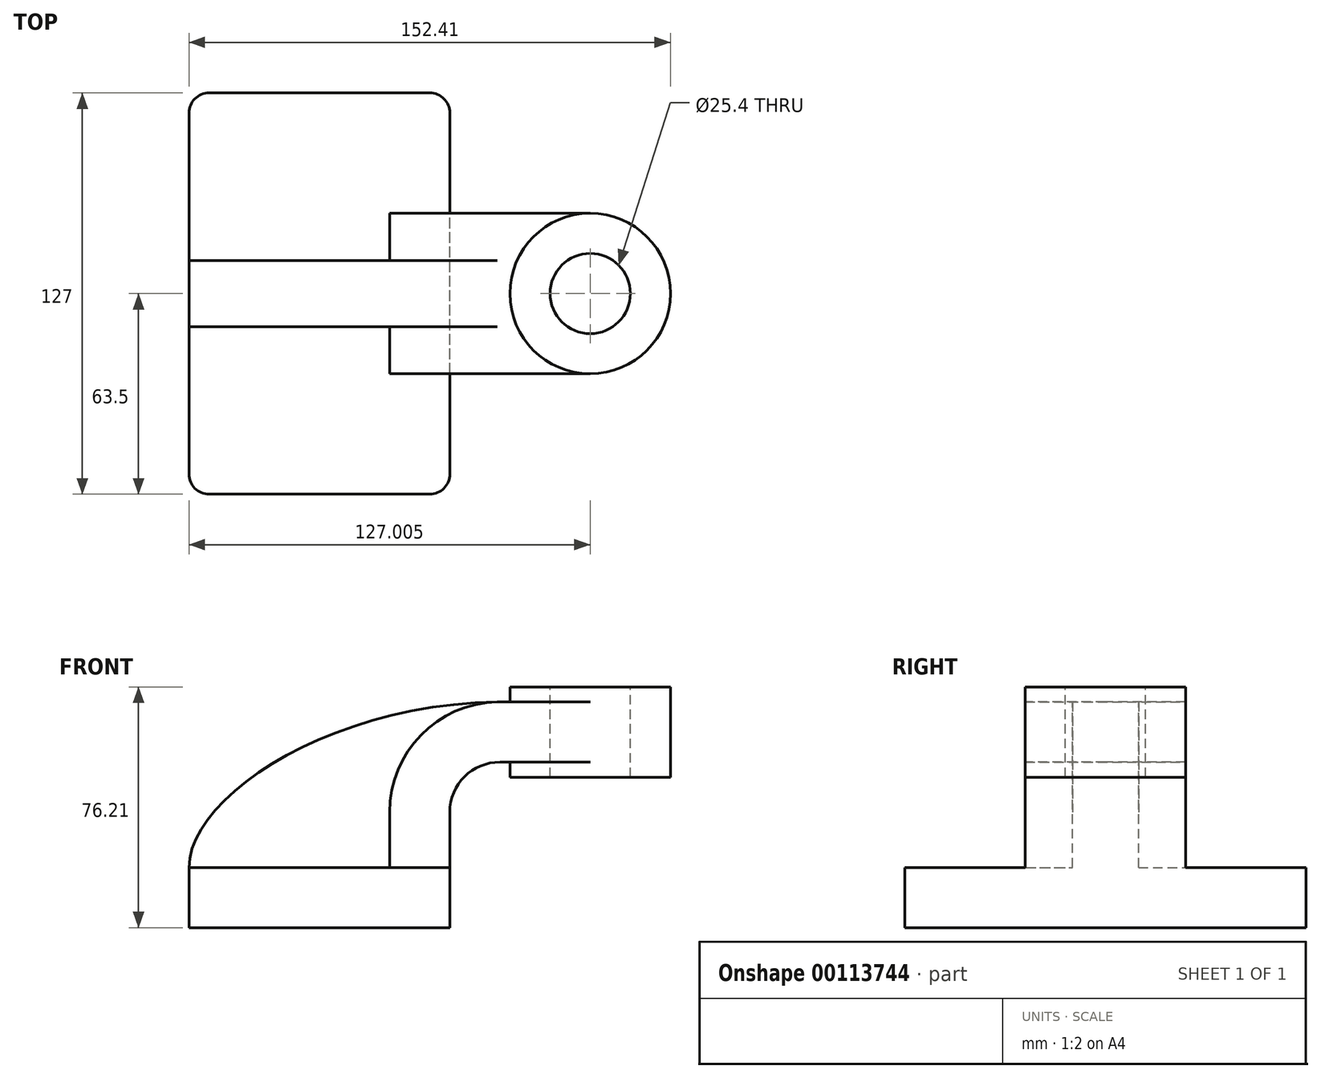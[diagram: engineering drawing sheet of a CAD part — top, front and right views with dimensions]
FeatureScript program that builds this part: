
annotation { "Feature Type Name" : "Feature", "Feature Type Description" : "" }
export const myFeature = defineFeature(function(context is Context, id is Id, definition is map)
    precondition{}
    {
        {
            var Q0;
            Q0=qCreatedBy(makeId("Front.planeOp"),FACE);
            var sketch = newSketch(context, id + "F0", { "sketchPlane" : qUnion([Q0])});
            skLineSegment(sketch, "E0.bottom", {"start": v(-41.28, -9.53) * mm, "end": v(41.28, -9.53) * mm});
            skLineSegment(sketch, "E0.top", {"start": v(-41.28, 9.53) * mm, "end": v(41.28, 9.53) * mm});
            skLineSegment(sketch, "E0.left", {"start": v(-41.28, -9.53) * mm, "end": v(-41.28, 9.53) * mm});
            skLineSegment(sketch, "E0.right", {"start": v(41.28, -9.53) * mm, "end": v(41.28, 9.53) * mm});
            skPoint(sketch, "E0.middle", {"position": v(0, 0) * mm});
            skLineSegment(sketch, "E1.bottom", {"start": v(60.32, 38.1) * mm, "end": v(111.12, 38.1) * mm});
            skLineSegment(sketch, "E1.top", {"start": v(60.32, 66.67) * mm, "end": v(111.12, 66.67) * mm});
            skLineSegment(sketch, "E1.left", {"start": v(60.32, 38.1) * mm, "end": v(60.32, 66.67) * mm});
            skLineSegment(sketch, "E1.right", {"start": v(111.12, 38.1) * mm, "end": v(111.12, 66.67) * mm});
            skPoint(sketch, "E1.middle", {"position": v(85.72, 52.39) * mm});
            skLineSegment(sketch, "E2", {"start": v(41.28, 9.53) * mm, "end": v(41.28, 27) * mm});
            skArc(sketch, "E3", {"start": v(41.27, 27) * mm, "mid": v(45.92, 38.23) * mm, "end": v(57.15, 42.88) * mm});
            skLineSegment(sketch, "E4", {"start": v(57.15, 42.88) * mm, "end": v(85.95, 42.88) * mm});
            skLineSegment(sketch, "E5.0", {"start": v(57.15, 61.93) * mm, "end": v(85.95, 61.93) * mm});
            skArc(sketch, "E5.1", {"start": v(22.22, 27) * mm, "mid": v(32.45, 51.7) * mm, "end": v(57.15, 61.93) * mm});
            skLineSegment(sketch, "E5.2", {"start": v(22.22, 9.53) * mm, "end": v(22.22, 27) * mm});
            skLineSegment(sketch, "E6", {"start": v(85.72, 38.1) * mm, "end": v(85.72, 66.67) * mm});
            skFitSpline(sketch, "E7", {"points": [v(-41.28, 9.53) * mm, v(57.15, 61.93) * mm], "startDerivative": vector(-0.06, 66.53) * mm, "endDerivative": vector(162.77, 1.47) * mm});
            skSolve(sketch);
        }
        {
            var Q0;
            Q0=makeQuery(id+"F0.imprint","IMPRINT",FACE,{"disambiguationData":[TD([[makeQuery(id+"F0.imprint","IMPRINT",EDGE,{"derivedFrom":sQuery(id+"F0.wireOp",EDGE,"E0.bottom")}),1.0]])]});
            extrude(context, id + "F1", {"entities" : qUnion([Q0]), "endBound" : BoundingType.SYMMETRIC, "depth" : 127 * mm});
        }
        {
            var Q0;
            {var subQ0=sQuery(id+"F0.wireOp",EDGE,"E4");var subQ1=sQuery(id+"F0.wireOp",EDGE,"E1.left");var subQ2=makeQuery(id+"F0.imprint","INTERSECT",VERTEX,{"derivedFrom":[subQ1,subQ0]});Q0=makeQuery(id+"F0.imprint","IMPRINT",FACE,{"disambiguationData":[TD([[makeQuery(id+"F0.imprint","IMPRINT",EDGE,{"disambiguationData":[TD([[subQ2,-1.0]])],"derivedFrom":subQ1}),-1.0]])]});}
            var Q1;
            {var subQ1=sQuery(id+"F0.wireOp",EDGE,"E2");Q1=makeQuery(id+"F0.imprint","IMPRINT",FACE,{"disambiguationData":[TD([[makeQuery(id+"F0.imprint","IMPRINT",EDGE,{"derivedFrom":subQ1}),1.0]])]});}
            extrude(context, id + "F2", {"entities" : qUnion([Q0, Q1]), "operationType" : NewBodyOperationType.ADD, "endBound" : BoundingType.SYMMETRIC, "depth" : 50.8 * mm});
        }
        {
            var Q0;
            {var subQ3=sQuery(id+"F0.wireOp",EDGE,"E5.2");Q0=makeQuery(id+"F0.imprint","IMPRINT",FACE,{"disambiguationData":[TD([[makeQuery(id+"F0.imprint","IMPRINT",EDGE,{"derivedFrom":subQ3}),1.0]])]});}
            extrude(context, id + "F3", {"entities" : qUnion([Q0]), "operationType" : NewBodyOperationType.ADD, "endBound" : BoundingType.SYMMETRIC, "depth" : 20.95 * mm});
        }
        {
            var Q0;
            {var subQ0=sQuery(id+"F0.wireOp",EDGE,"E1.right");Q0=makeQuery(id+"F0.imprint","IMPRINT",FACE,{"disambiguationData":[TD([[makeQuery(id+"F0.imprint","IMPRINT",EDGE,{"derivedFrom":subQ0}),1.0]])]});}
            var Q1;
            Q1=sQuery(id+"F0.wireOp",EDGE,"E6");
            revolve(context, id + "F4", {"operationType" : NewBodyOperationType.ADD, "entities" : qUnion([Q0]), "axis" : qUnion([Q1]), "revolveType" : RevolveType.FULL});
        }
        {
            var Q0;
            Q0=makeQuery(id+"F1.opExtrude","CAP_EDGE",EDGE,{"disambiguationData":[OSD([sQuery(id+"F0.wireOp",EDGE,"E0.left")])],"isStart":false});
            var Q1;
            Q1=makeQuery(id+"F1.opExtrude","CAP_EDGE",EDGE,{"disambiguationData":[OSD([sQuery(id+"F0.wireOp",EDGE,"E0.right")])],"isStart":false});
            var Q2;
            Q2=makeQuery(id+"F1.opExtrude","CAP_EDGE",EDGE,{"disambiguationData":[OSD([sQuery(id+"F0.wireOp",EDGE,"E0.right")])],"isStart":true});
            var Q3;
            Q3=makeQuery(id+"F1.opExtrude","CAP_EDGE",EDGE,{"disambiguationData":[OSD([sQuery(id+"F0.wireOp",EDGE,"E0.left")])],"isStart":true});
            fillet(context, id + "F5", {"entities" : qUnion([Q0, Q1, Q2, Q3]), "radius" : 6.35 * mm, "tangentPropagation" : true, "allowEdgeOverflow" : false});
        }
        {
            var Q0;
            Q0=makeQuery(id+"F4.opRevolve","SWEPT_FACE",FACE,{"disambiguationData":[OSD([sQuery(id+"F0.wireOp",EDGE,"E1.top")])]});
            var sketch = newSketch(context, id + "F6", { "sketchPlane" : qUnion([Q0])});
            skPoint(sketch, "E8", {"position": v(85.72, 0) * mm});
            skSolve(sketch);
        }
        {
            var Q0;
            Q0=sQuery(id+"F6.wireOp",VERTEX,"E8");
            var Q1;
            Q1=makeQuery(id+"F1.opExtrude","SWEPT_BODY",BODY,{"disambiguationData":[OSD([sQuery(id+"F0.wireOp",EDGE,"E0.bottom"),sQuery(id+"F0.wireOp",EDGE,"E0.top"),sQuery(id+"F0.wireOp",EDGE,"E0.left"),sQuery(id+"F0.wireOp",EDGE,"E0.right")])]});
            hole(context, id + "F7", {"style" : HoleStyle.SIMPLE, "endStyle" : HoleEndStyle.THROUGH, "holeDiameter" : 25.4 * mm, "locations" : qUnion([Q0]), "scope" : qUnion([Q1]), "isTappedThrough" : true});
        }
    });
